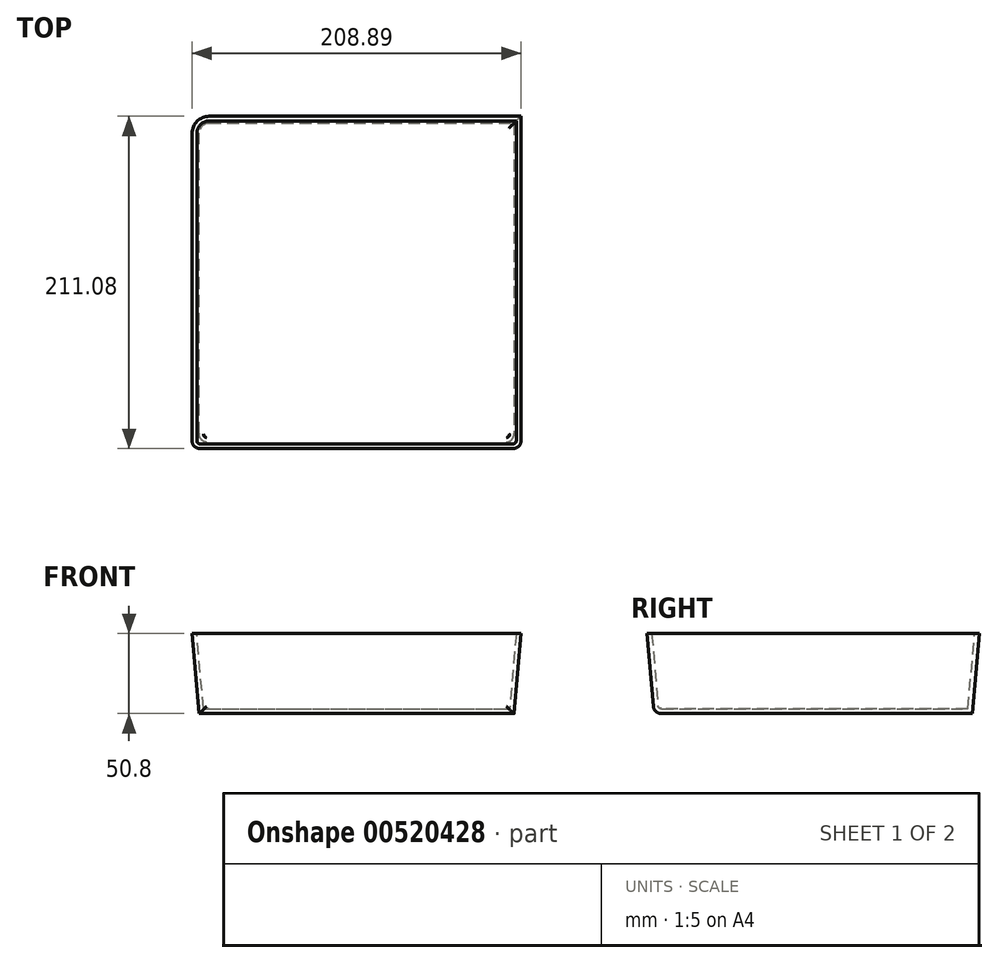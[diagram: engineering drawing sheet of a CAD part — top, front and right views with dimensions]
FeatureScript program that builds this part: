
annotation { "Feature Type Name" : "Feature", "Feature Type Description" : "" }
export const myFeature = defineFeature(function(context is Context, id is Id, definition is map)
    precondition{}
    {
        {
            var Q0;
            Q0=qCreatedBy(makeId("Top.planeOp"),FACE);
            var sketch = newSketch(context, id + "F0", { "sketchPlane" : qUnion([Q0])});
            skLineSegment(sketch, "E0", {"start": v(-88.27, 95.55) * mm, "end": v(105.38, 95.55) * mm});
            skLineSegment(sketch, "E1", {"start": v(105.38, 95.55) * mm, "end": v(105.38, -106.64) * mm});
            skLineSegment(sketch, "E2", {"start": v(105.38, -106.64) * mm, "end": v(-94.62, -106.64) * mm});
            skLineSegment(sketch, "E3", {"start": v(-94.62, -106.64) * mm, "end": v(-94.62, 89.2) * mm});
            skPoint(sketch, "E4.visualSharp", {"position": v(-94.62, 95.55) * mm});
            skArc(sketch, "E4.filletArc", {"start": v(-88.27, 95.55) * mm, "mid": v(-92.76, 93.7) * mm, "end": v(-94.62, 89.2) * mm});
            skSolve(sketch);
        }
        {
            var Q0;
            Q0 = qSketchRegion(id + "F0", true);
            var sketch = newSketch(context, id + "F1", { "sketchPlane" : qUnion([Q0])});
            skSolve(sketch);
        }
        {
            var Q0;
            Q0 = qSketchRegion(id + "F1", true);
            var Q1;
            Q1=makeQuery(id+"F0.imprint","IMPRINT",FACE,{"disambiguationData":[TD([[makeQuery(id+"F0.imprint","IMPRINT",EDGE,{"derivedFrom":sQuery(id+"F0.wireOp",EDGE,"E0")}),-1.0]])]});
            extrude(context, id + "F2", {"entities" : qUnion([Q0, Q1]), "depth" : 50.8 * mm, "offsetDistance" : 25.4 * mm, "hasDraft" : true, "draftAngle" : 5 * degree});
        }
        {
            var Q0;
            Q0=makeQuery(id+"F2.opExtrude","CAP_EDGE",EDGE,{"disambiguationData":[OSD([sQuery(id+"F0.wireOp",EDGE,"E2")])],"isStart":true});
            var Q1;
            Q1=makeQuery(id+"F2.opExtrude","SWEPT_EDGE",EDGE,{"disambiguationData":[OSD([sQuery(id+"F0.wireOp",EDGE,"E2"),sQuery(id+"F0.wireOp",EDGE,"E3")])]});
            var Q2;
            Q2=makeQuery(id+"F2.opExtrude","SWEPT_EDGE",EDGE,{"disambiguationData":[OSD([sQuery(id+"F0.wireOp",EDGE,"E3"),sQuery(id+"F0.wireOp",EDGE,"E4.filletArc")])]});
            var Q3;
            Q3=makeQuery(id+"F2.opExtrude","SWEPT_EDGE",EDGE,{"disambiguationData":[OSD([sQuery(id+"F0.wireOp",EDGE,"E1"),sQuery(id+"F0.wireOp",EDGE,"E2")])]});
            fillet(context, id + "F3", {"entities" : qUnion([Q0, Q1, Q2, Q3]), "radius" : 5.08 * mm, "tangentPropagation" : true, "allowEdgeOverflow" : false});
        }
        {
            var Q0;
            Q0=makeQuery(id+"F2.opExtrude","CAP_FACE",FACE,{"disambiguationData":[OSD([sQuery(id+"F0.wireOp",EDGE,"E0"),sQuery(id+"F0.wireOp",EDGE,"E1"),sQuery(id+"F0.wireOp",EDGE,"E2"),sQuery(id+"F0.wireOp",EDGE,"E3"),sQuery(id+"F0.wireOp",EDGE,"E4.filletArc")])],"isStart":false});
            shell(context, id + "F4", {"entities" : qUnion([Q0]), "thickness" : 3 * mm});
        }
        {
            var Q0;
            {var subQ0=sQuery(id+"F0.wireOp",EDGE,"E0");Q0=makeQuery(id+"F4.opShell","OFFSET_EDGE",EDGE,{"disambiguationData":[OSD([subQ0]),TDD([makeQuery(id+"F2.opExtrude","CAP_EDGE",EDGE,{"disambiguationData":[OSD([subQ0])],"isStart":true})])]});}
            var Q1;
            Q1=makeQuery(id+"F4.opShell","OFFSET_FACE",FACE,{"disambiguationData":[OSD([sQuery(id+"F0.wireOp",EDGE,"E0"),sQuery(id+"F0.wireOp",EDGE,"E1"),sQuery(id+"F0.wireOp",EDGE,"E2"),sQuery(id+"F0.wireOp",EDGE,"E3"),sQuery(id+"F0.wireOp",EDGE,"E4.filletArc")])]});
            fillet(context, id + "F5", {"entities" : qUnion([Q0, Q1]), "radius" : 0.2 * mm, "tangentPropagation" : true, "allowEdgeOverflow" : false});
        }
    });
